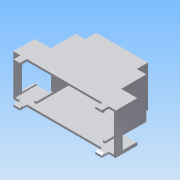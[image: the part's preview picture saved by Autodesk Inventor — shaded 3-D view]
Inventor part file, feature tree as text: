
AUTODESK INVENTOR PART (.ipt)
format: ipt  version: 2015 SP1 (Build 190203100, 203)  size: 469,504 bytes
history: native  units: mm
features: extrude x14, sketch x14, fillet x5, other x4, mirror x2, projected_geometry x1
ambient origin geometry x8: Origin, YZ Plane, XZ Plane, XY Plane, X Axis, Y Axis, Z Axis, Center Point
bodies: Body1 (feature_tree)
feature tree (40):
  other  "Твердое тело1"
  extrude  "Выдавливание1"  Depth=90.2mm
  other  "РабПлоскость1"
  extrude  "Выдавливание2"  Depth=22.35mm
  extrude  "Выдавливание3"  Depth=19.0mm
  extrude  "Выдавливание4"  Depth=50.7mm
  extrude  "Выдавливание5"  Depth=14.1mm
  extrude  "Выдавливание6"  Depth=14.1mm
  extrude  "Выдавливание7"  Depth=62.0mm
  mirror  "Зеркальное отражение2"
  extrude  "Выдавливание8"  Depth=45.5mm
  other  "РабПлоскость2"
  extrude  "Выдавливание9"  Depth=50.7mm
  extrude  "Выдавливание10"  Depth=19.0mm
  extrude  "Выдавливание11"  Depth=41.0mm
  fillet  "Сопряжение1"  Radius=1.75mm
  fillet  "Сопряжение2"  Radius=36.3mm
  fillet  "Сопряжение3"  Radius=1.75mm
  fillet  "Сопряжение4"  Radius=6.0mm
  extrude  "Выдавливание12"  Depth=3.0mm
  extrude  "Выдавливание13"  Depth=3.0mm
  extrude  "Выдавливание14"  Depth=1.7mm TaperAngle=0.0deg
  other  "РабПлоскость3"
  mirror  "Зеркальное отражение3"
  fillet  "Сопряжение5"  Radius=1.8mm
  sketch  "Эскиз1"
  sketch  "Эскиз2"
  projected_geometry  "Спроецированная петля1"
  sketch  "Эскиз3"
  sketch  "Эскиз4"
  sketch  "Эскиз5"
  sketch  "Эскиз6"
  sketch  "Эскиз7"
  sketch  "Эскиз8"
  sketch  "Эскиз9"
  sketch  "Эскиз10"
  sketch  "Эскиз11"
  sketch  "Эскиз12"
  sketch  "Эскиз13"
  sketch  "Эскиз14"
